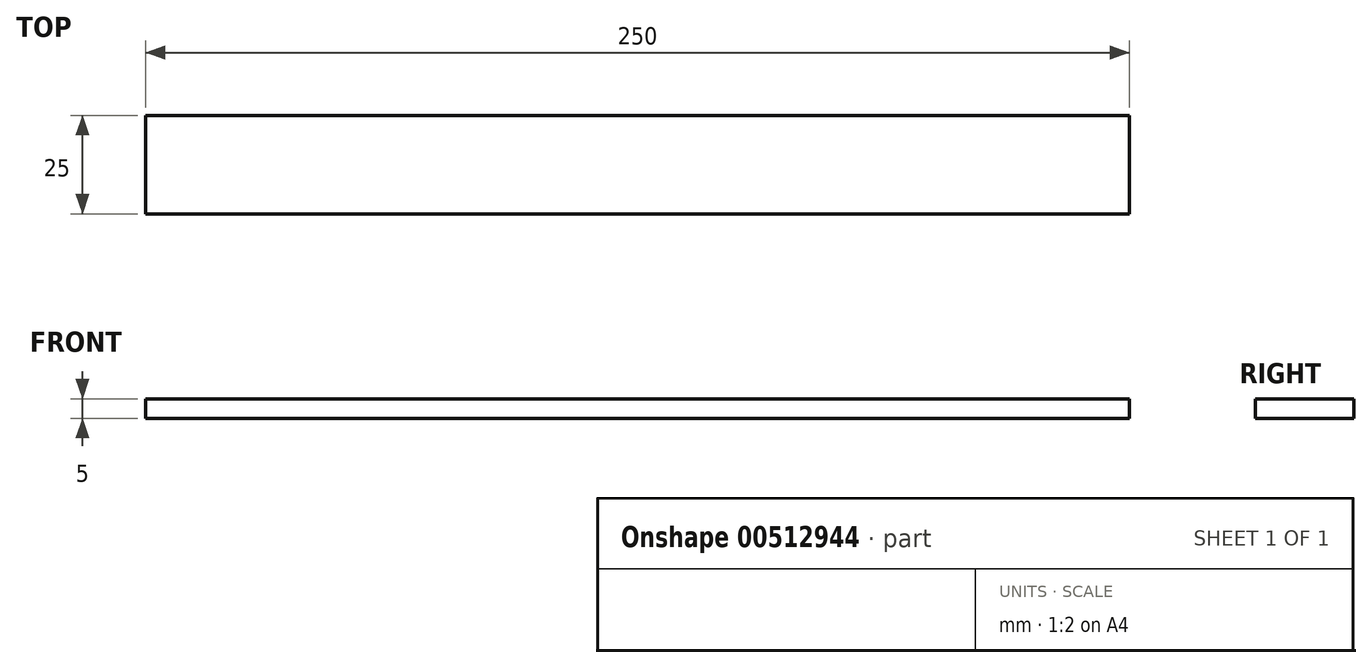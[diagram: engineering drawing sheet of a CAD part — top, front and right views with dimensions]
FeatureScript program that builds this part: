
annotation { "Feature Type Name" : "Feature", "Feature Type Description" : "" }
export const myFeature = defineFeature(function(context is Context, id is Id, definition is map)
    precondition{}
    {
        {
            var Q0;
            Q0=qCreatedBy(makeId("Top.planeOp"),FACE);
            var sketch = newSketch(context, id + "F0", { "sketchPlane" : qUnion([Q0])});
            skLineSegment(sketch, "E0.bottom", {"start": v(0, 0) * mm, "end": v(250, 0) * mm});
            skLineSegment(sketch, "E0.top", {"start": v(0, 25) * mm, "end": v(250, 25) * mm});
            skLineSegment(sketch, "E0.left", {"start": v(0, 0) * mm, "end": v(0, 25) * mm});
            skLineSegment(sketch, "E0.right", {"start": v(250, 0) * mm, "end": v(250, 25) * mm});
            skSolve(sketch);
        }
        {
            var Q0;
            Q0 = qSketchRegion(id + "F0", true);
            extrude(context, id + "F1", {"entities" : qUnion([Q0]), "depth" : 5 * mm});
        }
    });
